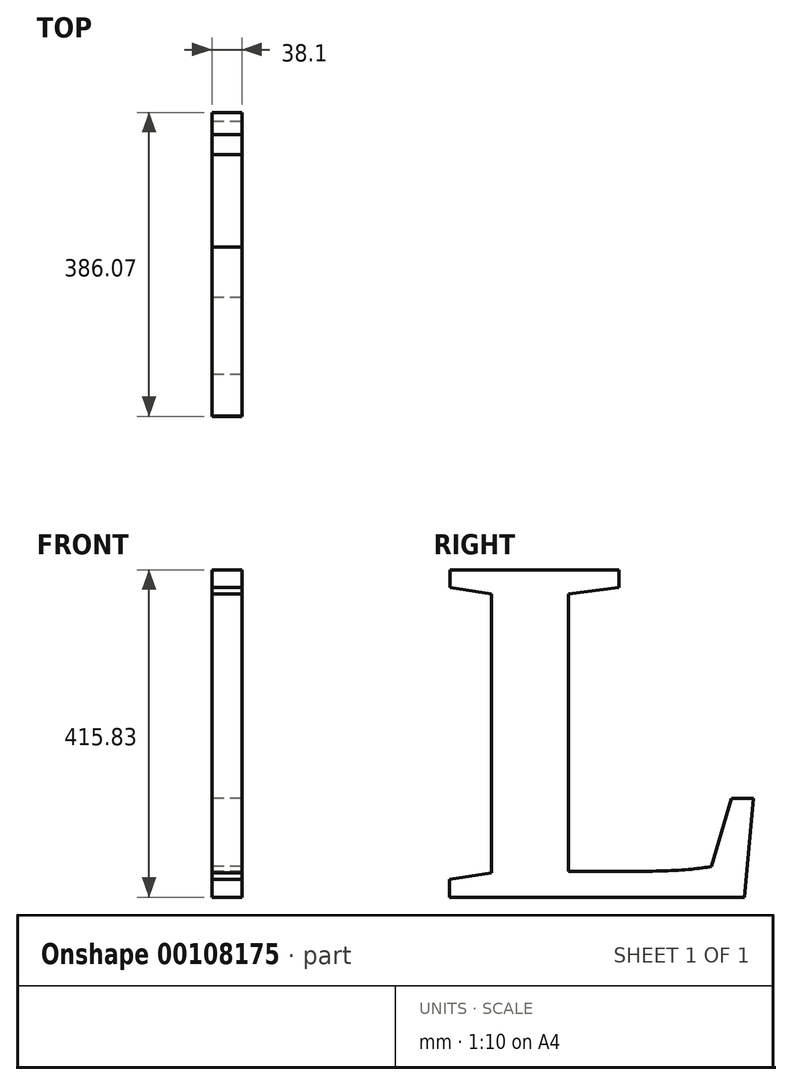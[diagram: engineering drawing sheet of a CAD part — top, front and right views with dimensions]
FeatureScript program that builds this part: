
annotation { "Feature Type Name" : "Feature", "Feature Type Description" : "" }
export const myFeature = defineFeature(function(context is Context, id is Id, definition is map)
    precondition{}
    {
        {
            var Q0;
            Q0=qCreatedBy(makeId("Right.planeOp"),FACE);
            var sketch = newSketch(context, id + "F0", { "sketchPlane" : qUnion([Q0])});
            skText(sketch, "E0", { "text": "L", "fontName": "Tinos-Bold.ttf"});
            const initialGuessF0  = {"E0": [-0.43656, 0, 1, 0, 0.4572]};
            skSetInitialGuess(sketch, initialGuessF0);
            skSolve(sketch);
        }
        {
            var Q0;
            Q0 = qSketchRegion(id + "F0", true);
            extrude(context, id + "F1", {"entities" : qUnion([Q0]), "depth" : 38.1 * mm});
        }
    });
